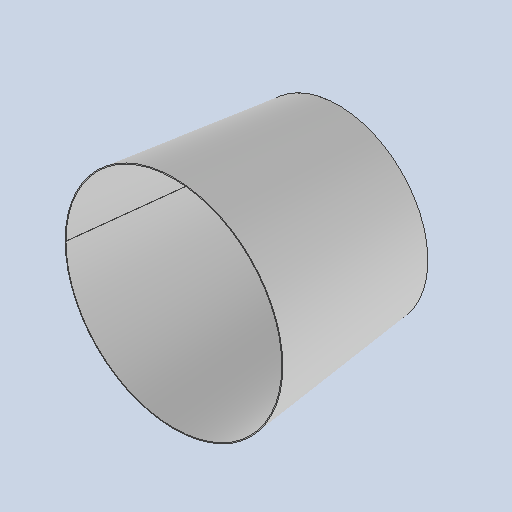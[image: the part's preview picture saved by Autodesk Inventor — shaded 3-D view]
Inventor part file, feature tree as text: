
AUTODESK INVENTOR PART (.ipt)
format: ipt  version: 2025 (Build 290162010, 162A)  size: 150,016 bytes
history: native  units: mm
features: other x2, revolve x1, sketch x1
ambient origin geometry x8: Origin, YZ Plane, XZ Plane, XY Plane, X Axis, Y Axis, Z Axis, Center Point
bodies: Solid1 (feature_tree)
feature tree (4):
  revolve  "Revolution1"  [1 undecoded]
  other  "A-Side Definition"
  sketch  "Sketch1"  dims[d0=151.0mm d3=62.8144mm d4=200.0mm d6=165.0mm d7=0.8mm]
  other  "Definition1"
note: 1 required parameter value undecoded (feature->parameter linkage not recoverable at this tier; creation-order binding heuristic only, values carry confidence <= 0.55)
